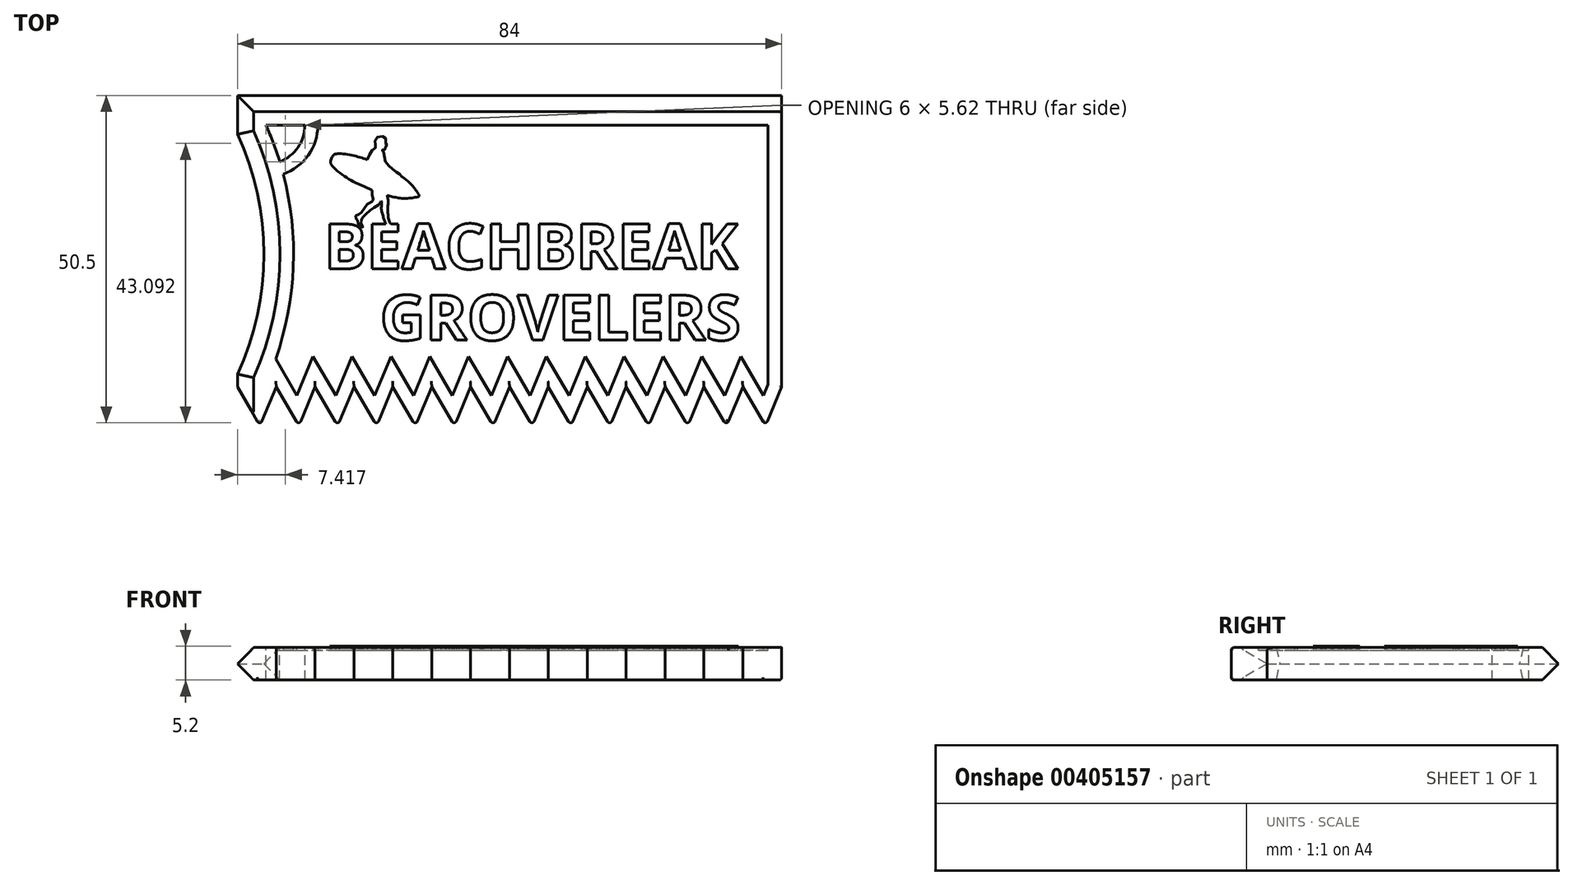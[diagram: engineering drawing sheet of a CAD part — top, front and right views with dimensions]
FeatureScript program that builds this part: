
annotation { "Feature Type Name" : "Feature", "Feature Type Description" : "" }
export const myFeature = defineFeature(function(context is Context, id is Id, definition is map)
    precondition{}
    {
        {
            assignVariable(context, id + "F0", {"name" : "t", "anyValue" : 2});
        }
        {
            var Q0;
            Q0=qCreatedBy(makeId("Top.planeOp"),FACE);
            var sketch = newSketch(context, id + "F1", { "sketchPlane" : qUnion([Q0])});
            skLineSegment(sketch, "E0.bottom", {"start": v(84, 51) * mm, "end": v(0, 51) * mm});
            skLineSegment(sketch, "E0.top", {"start": v(81.5, 0) * mm, "end": v(3.5, 0) * mm, "construction": true});
            skLineSegment(sketch, "E0.left", {"start": v(84, 51) * mm, "end": v(84, 6) * mm});
            skLineSegment(sketch, "E0.right", {"start": v(0, 51) * mm, "end": v(0, 6) * mm, "construction": true});
            skLineSegment(sketch, "E1", {"start": v(84, 6) * mm, "end": v(0, 6) * mm, "construction": true});
            skLineSegment(sketch, "E2", {"start": v(84, 6) * mm, "end": v(81.5, 0) * mm});
            skLineSegment(sketch, "E3", {"start": v(81.5, 0) * mm, "end": v(78, 6) * mm});
            skLineSegment(sketch, "E4.1.0.0", {"start": v(78, 6) * mm, "end": v(75.5, 0) * mm});
            skLineSegment(sketch, "E4.1.0.1", {"start": v(75.5, 0) * mm, "end": v(72, 6) * mm});
            skLineSegment(sketch, "E4.2.0.0", {"start": v(72, 6) * mm, "end": v(69.5, 0) * mm});
            skLineSegment(sketch, "E4.2.0.1", {"start": v(69.5, 0) * mm, "end": v(66, 6) * mm});
            skLineSegment(sketch, "E4.3.0.0", {"start": v(66, 6) * mm, "end": v(63.5, 0) * mm});
            skLineSegment(sketch, "E4.3.0.1", {"start": v(63.5, 0) * mm, "end": v(60, 6) * mm});
            skLineSegment(sketch, "E4.4.0.0", {"start": v(60, 6) * mm, "end": v(57.5, 0) * mm});
            skLineSegment(sketch, "E4.4.0.1", {"start": v(57.5, 0) * mm, "end": v(54, 6) * mm});
            skLineSegment(sketch, "E4.5.0.0", {"start": v(54, 6) * mm, "end": v(51.5, 0) * mm});
            skLineSegment(sketch, "E4.5.0.1", {"start": v(51.5, 0) * mm, "end": v(48, 6) * mm});
            skLineSegment(sketch, "E4.6.0.0", {"start": v(48, 6) * mm, "end": v(45.5, 0) * mm});
            skLineSegment(sketch, "E4.6.0.1", {"start": v(45.5, 0) * mm, "end": v(42, 6) * mm});
            skLineSegment(sketch, "E4.7.0.0", {"start": v(42, 6) * mm, "end": v(39.5, 0) * mm});
            skLineSegment(sketch, "E4.7.0.1", {"start": v(39.5, 0) * mm, "end": v(36, 6) * mm});
            skLineSegment(sketch, "E4.8.0.0", {"start": v(36, 6) * mm, "end": v(33.5, 0) * mm});
            skLineSegment(sketch, "E4.8.0.1", {"start": v(33.5, 0) * mm, "end": v(30, 6) * mm});
            skLineSegment(sketch, "E4.9.0.0", {"start": v(30, 6) * mm, "end": v(27.5, 0) * mm});
            skLineSegment(sketch, "E4.9.0.1", {"start": v(27.5, 0) * mm, "end": v(24, 6) * mm});
            skLineSegment(sketch, "E4.10.0.0", {"start": v(24, 6) * mm, "end": v(21.5, 0) * mm});
            skLineSegment(sketch, "E4.10.0.1", {"start": v(21.5, 0) * mm, "end": v(18, 6) * mm});
            skLineSegment(sketch, "E4.11.0.0", {"start": v(18, 6) * mm, "end": v(15.5, 0) * mm});
            skLineSegment(sketch, "E4.11.0.1", {"start": v(15.5, 0) * mm, "end": v(12, 6) * mm});
            skLineSegment(sketch, "E4.12.0.0", {"start": v(12, 6) * mm, "end": v(9.5, 0) * mm});
            skLineSegment(sketch, "E4.12.0.1", {"start": v(9.5, 0) * mm, "end": v(6, 6) * mm});
            skLineSegment(sketch, "E4.13.0.0", {"start": v(6, 6) * mm, "end": v(3.5, 0) * mm});
            skLineSegment(sketch, "E4.13.0.1", {"start": v(3.5, 0) * mm, "end": v(0, 6) * mm});
            skLineSegment(sketch, "E4.direction1", {"start": v(84, 6) * mm, "end": v(78, 6) * mm, "construction": true});
            skLineSegment(sketch, "E5", {"start": v(0, 6) * mm, "end": v(0, 8) * mm});
            skArc(sketch, "E6", {"start": v(0, 8) * mm, "mid": v(4.07, 26.5) * mm, "end": v(0, 45) * mm});
            skLineSegment(sketch, "E7", {"start": v(0, 45) * mm, "end": v(0, 51) * mm});
            skLineSegment(sketch, "E8", {"start": v(0, 6) * mm, "end": v(0, 0) * mm, "construction": true});
            skSolve(sketch);
        }
        {
            var Q0;
            Q0=qSketchRegion(id+"F1",true);
            extrude(context, id + "F2", {"entities" : qUnion([Q0]), "depth" : 5 * mm});
        }
        {
            var Q0;
            Q0=makeQuery(id+"F2.opExtrude","CAP_EDGE",EDGE,{"disambiguationData":[OSD([sQuery(id+"F1.wireOp",EDGE,"E5")])],"isStart":false});
            var Q1;
            Q1=makeQuery(id+"F2.opExtrude","CAP_EDGE",EDGE,{"disambiguationData":[OSD([sQuery(id+"F1.wireOp",EDGE,"E6")])],"isStart":false});
            var Q2;
            Q2=makeQuery(id+"F2.opExtrude","CAP_EDGE",EDGE,{"disambiguationData":[OSD([sQuery(id+"F1.wireOp",EDGE,"E0.bottom")])],"isStart":false});
            var Q3;
            Q3=makeQuery(id+"F2.opExtrude","CAP_EDGE",EDGE,{"disambiguationData":[OSD([sQuery(id+"F1.wireOp",EDGE,"E7")])],"isStart":false});
            var Q4;
            Q4=makeQuery(id+"F2.opExtrude","CAP_EDGE",EDGE,{"disambiguationData":[OSD([sQuery(id+"F1.wireOp",EDGE,"E0.bottom")])],"isStart":true});
            var Q5;
            Q5=makeQuery(id+"F2.opExtrude","CAP_EDGE",EDGE,{"disambiguationData":[OSD([sQuery(id+"F1.wireOp",EDGE,"E7")])],"isStart":true});
            var Q6;
            Q6=makeQuery(id+"F2.opExtrude","CAP_EDGE",EDGE,{"disambiguationData":[OSD([sQuery(id+"F1.wireOp",EDGE,"E6")])],"isStart":true});
            var Q7;
            Q7=makeQuery(id+"F2.opExtrude","CAP_EDGE",EDGE,{"disambiguationData":[OSD([sQuery(id+"F1.wireOp",EDGE,"E5")])],"isStart":true});
            chamfer(context, id + "F3", {"entities" : qUnion([Q0, Q1, Q2, Q3, Q4, Q5, Q6, Q7]), "chamferType" : ChamferType.TWO_OFFSETS, "width1" : 2.5 * mm, "oppositeDirection" : false, "width2" : 2.5 * mm, "tangentPropagation" : true});
        }
        {
            var Q0;
            Q0=makeQuery(id+"F2.opExtrude","CAP_FACE",FACE,{"disambiguationData":[OSD([sQuery(id+"F1.wireOp",EDGE,"E0.bottom"),sQuery(id+"F1.wireOp",EDGE,"E0.left"),sQuery(id+"F1.wireOp",EDGE,"E2"),sQuery(id+"F1.wireOp",EDGE,"E3"),sQuery(id+"F1.wireOp",EDGE,"E4.1.0.0"),sQuery(id+"F1.wireOp",EDGE,"E4.1.0.1"),sQuery(id+"F1.wireOp",EDGE,"E4.2.0.0"),sQuery(id+"F1.wireOp",EDGE,"E4.2.0.1"),sQuery(id+"F1.wireOp",EDGE,"E4.3.0.0"),sQuery(id+"F1.wireOp",EDGE,"E4.3.0.1"),sQuery(id+"F1.wireOp",EDGE,"E4.4.0.0"),sQuery(id+"F1.wireOp",EDGE,"E4.4.0.1"),sQuery(id+"F1.wireOp",EDGE,"E4.5.0.0"),sQuery(id+"F1.wireOp",EDGE,"E4.5.0.1"),sQuery(id+"F1.wireOp",EDGE,"E4.6.0.0"),sQuery(id+"F1.wireOp",EDGE,"E4.6.0.1"),sQuery(id+"F1.wireOp",EDGE,"E4.7.0.0"),sQuery(id+"F1.wireOp",EDGE,"E4.7.0.1"),sQuery(id+"F1.wireOp",EDGE,"E4.8.0.0"),sQuery(id+"F1.wireOp",EDGE,"E4.8.0.1"),sQuery(id+"F1.wireOp",EDGE,"E4.9.0.0"),sQuery(id+"F1.wireOp",EDGE,"E4.9.0.1"),sQuery(id+"F1.wireOp",EDGE,"E4.10.0.0"),sQuery(id+"F1.wireOp",EDGE,"E4.10.0.1"),sQuery(id+"F1.wireOp",EDGE,"E4.11.0.0"),sQuery(id+"F1.wireOp",EDGE,"E4.11.0.1"),sQuery(id+"F1.wireOp",EDGE,"E4.12.0.0"),sQuery(id+"F1.wireOp",EDGE,"E4.12.0.1"),sQuery(id+"F1.wireOp",EDGE,"E4.13.0.0"),sQuery(id+"F1.wireOp",EDGE,"E4.13.0.1"),sQuery(id+"F1.wireOp",EDGE,"E5"),sQuery(id+"F1.wireOp",EDGE,"E6"),sQuery(id+"F1.wireOp",EDGE,"E7")])],"isStart":false});
            var sketch = newSketch(context, id + "F4", { "sketchPlane" : qUnion([Q0])});
            skLineSegment(sketch, "E9.0", {"start": v(81.9, 6.42) * mm, "end": v(81.9, 46.4) * mm});
            skLineSegment(sketch, "E9.1", {"start": v(81.19, 4.7) * mm, "end": v(81.9, 6.42) * mm});
            skLineSegment(sketch, "E9.2", {"start": v(77.69, 10.7) * mm, "end": v(81.19, 4.7) * mm});
            skLineSegment(sketch, "E9.3", {"start": v(75.19, 4.7) * mm, "end": v(77.69, 10.7) * mm});
            skLineSegment(sketch, "E9.4", {"start": v(71.69, 10.7) * mm, "end": v(75.19, 4.7) * mm});
            skLineSegment(sketch, "E9.5", {"start": v(69.19, 4.7) * mm, "end": v(71.69, 10.7) * mm});
            skLineSegment(sketch, "E9.6", {"start": v(65.69, 10.7) * mm, "end": v(69.19, 4.7) * mm});
            skLineSegment(sketch, "E9.7", {"start": v(81.9, 46.4) * mm, "end": v(4.42, 46.4) * mm});
            skArc(sketch, "E9.8", {"start": v(4.42, 46.4) * mm, "mid": v(8.63, 28.5) * mm, "end": v(5.9, 10.33) * mm});
            skLineSegment(sketch, "E9.9", {"start": v(5.9, 10.33) * mm, "end": v(9.19, 4.7) * mm});
            skLineSegment(sketch, "E9.10", {"start": v(9.19, 4.7) * mm, "end": v(11.69, 10.7) * mm});
            skLineSegment(sketch, "E9.11", {"start": v(11.69, 10.7) * mm, "end": v(15.19, 4.7) * mm});
            skLineSegment(sketch, "E9.12", {"start": v(15.19, 4.7) * mm, "end": v(17.69, 10.7) * mm});
            skLineSegment(sketch, "E9.13", {"start": v(17.69, 10.7) * mm, "end": v(21.19, 4.7) * mm});
            skLineSegment(sketch, "E9.14", {"start": v(21.19, 4.7) * mm, "end": v(23.69, 10.7) * mm});
            skLineSegment(sketch, "E9.15", {"start": v(23.69, 10.7) * mm, "end": v(27.19, 4.7) * mm});
            skLineSegment(sketch, "E9.16", {"start": v(27.19, 4.7) * mm, "end": v(29.69, 10.7) * mm});
            skLineSegment(sketch, "E9.17", {"start": v(29.69, 10.7) * mm, "end": v(33.19, 4.7) * mm});
            skLineSegment(sketch, "E9.18", {"start": v(33.19, 4.7) * mm, "end": v(35.69, 10.7) * mm});
            skLineSegment(sketch, "E9.19", {"start": v(35.69, 10.7) * mm, "end": v(39.19, 4.7) * mm});
            skLineSegment(sketch, "E9.20", {"start": v(39.19, 4.7) * mm, "end": v(41.69, 10.7) * mm});
            skLineSegment(sketch, "E9.21", {"start": v(41.69, 10.7) * mm, "end": v(45.19, 4.7) * mm});
            skLineSegment(sketch, "E9.22", {"start": v(45.19, 4.7) * mm, "end": v(47.69, 10.7) * mm});
            skLineSegment(sketch, "E9.23", {"start": v(47.69, 10.7) * mm, "end": v(51.19, 4.7) * mm});
            skLineSegment(sketch, "E9.24", {"start": v(51.19, 4.7) * mm, "end": v(53.69, 10.7) * mm});
            skLineSegment(sketch, "E9.25", {"start": v(53.69, 10.7) * mm, "end": v(57.19, 4.7) * mm});
            skLineSegment(sketch, "E9.26", {"start": v(57.19, 4.7) * mm, "end": v(59.69, 10.7) * mm});
            skLineSegment(sketch, "E9.27", {"start": v(59.69, 10.7) * mm, "end": v(63.19, 4.7) * mm});
            skLineSegment(sketch, "E9.28", {"start": v(63.19, 4.7) * mm, "end": v(65.69, 10.7) * mm});
            skSolve(sketch);
        }
        {
            var Q0;
            Q0=makeQuery(id+"F4.imprint","IMPRINT",FACE,{"disambiguationData":[TD([[makeQuery(id+"F4.imprint","IMPRINT",EDGE,{"derivedFrom":sQuery(id+"F4.wireOp",EDGE,"E9.0")}),1.0]])]});
            extrude(context, id + "F5", {"entities" : qUnion([Q0]), "operationType" : NewBodyOperationType.REMOVE, "oppositeDirection" : true, "depth" : (getVariable(context, 't') / 5) * mm});
        }
        {
            var Q0;
            Q0=makeQuery(id+"F2.opExtrude","CAP_EDGE",EDGE,{"disambiguationData":[OSD([sQuery(id+"F1.wireOp",EDGE,"E4.13.0.1")])],"isStart":false});
            var Q1;
            Q1=makeQuery(id+"F2.opExtrude","CAP_EDGE",EDGE,{"disambiguationData":[OSD([sQuery(id+"F1.wireOp",EDGE,"E4.13.0.0")])],"isStart":false});
            var Q2;
            Q2=makeQuery(id+"F2.opExtrude","SWEPT_EDGE",EDGE,{"disambiguationData":[OSD([sQuery(id+"F1.wireOp",EDGE,"E4.13.0.0"),sQuery(id+"F1.wireOp",EDGE,"E4.13.0.1")])]});
            var Q3;
            Q3=makeQuery(id+"F2.opExtrude","CAP_EDGE",EDGE,{"disambiguationData":[OSD([sQuery(id+"F1.wireOp",EDGE,"E4.12.0.1")])],"isStart":false});
            var Q4;
            Q4=makeQuery(id+"F2.opExtrude","SWEPT_EDGE",EDGE,{"disambiguationData":[OSD([sQuery(id+"F1.wireOp",EDGE,"E4.12.0.0"),sQuery(id+"F1.wireOp",EDGE,"E4.12.0.1")])]});
            var Q5;
            Q5=makeQuery(id+"F2.opExtrude","CAP_EDGE",EDGE,{"disambiguationData":[OSD([sQuery(id+"F1.wireOp",EDGE,"E4.12.0.0")])],"isStart":false});
            var Q6;
            Q6=makeQuery(id+"F2.opExtrude","CAP_EDGE",EDGE,{"disambiguationData":[OSD([sQuery(id+"F1.wireOp",EDGE,"E4.11.0.1")])],"isStart":false});
            var Q7;
            Q7=makeQuery(id+"F2.opExtrude","SWEPT_EDGE",EDGE,{"disambiguationData":[OSD([sQuery(id+"F1.wireOp",EDGE,"E4.11.0.0"),sQuery(id+"F1.wireOp",EDGE,"E4.11.0.1")])]});
            var Q8;
            Q8=makeQuery(id+"F2.opExtrude","CAP_EDGE",EDGE,{"disambiguationData":[OSD([sQuery(id+"F1.wireOp",EDGE,"E4.11.0.0")])],"isStart":false});
            var Q9;
            Q9=makeQuery(id+"F2.opExtrude","CAP_EDGE",EDGE,{"disambiguationData":[OSD([sQuery(id+"F1.wireOp",EDGE,"E4.10.0.1")])],"isStart":false});
            var Q10;
            Q10=makeQuery(id+"F2.opExtrude","CAP_EDGE",EDGE,{"disambiguationData":[OSD([sQuery(id+"F1.wireOp",EDGE,"E4.10.0.0")])],"isStart":false});
            var Q11;
            Q11=makeQuery(id+"F2.opExtrude","CAP_EDGE",EDGE,{"disambiguationData":[OSD([sQuery(id+"F1.wireOp",EDGE,"E4.9.0.1")])],"isStart":false});
            var Q12;
            Q12=makeQuery(id+"F2.opExtrude","CAP_EDGE",EDGE,{"disambiguationData":[OSD([sQuery(id+"F1.wireOp",EDGE,"E4.9.0.0")])],"isStart":false});
            var Q13;
            Q13=makeQuery(id+"F2.opExtrude","CAP_EDGE",EDGE,{"disambiguationData":[OSD([sQuery(id+"F1.wireOp",EDGE,"E4.8.0.1")])],"isStart":false});
            var Q14;
            Q14=makeQuery(id+"F2.opExtrude","CAP_EDGE",EDGE,{"disambiguationData":[OSD([sQuery(id+"F1.wireOp",EDGE,"E4.8.0.0")])],"isStart":false});
            var Q15;
            Q15=makeQuery(id+"F2.opExtrude","CAP_EDGE",EDGE,{"disambiguationData":[OSD([sQuery(id+"F1.wireOp",EDGE,"E4.7.0.1")])],"isStart":false});
            var Q16;
            Q16=makeQuery(id+"F2.opExtrude","CAP_EDGE",EDGE,{"disambiguationData":[OSD([sQuery(id+"F1.wireOp",EDGE,"E4.7.0.0")])],"isStart":false});
            var Q17;
            Q17=makeQuery(id+"F2.opExtrude","CAP_EDGE",EDGE,{"disambiguationData":[OSD([sQuery(id+"F1.wireOp",EDGE,"E4.6.0.1")])],"isStart":false});
            var Q18;
            Q18=makeQuery(id+"F2.opExtrude","CAP_EDGE",EDGE,{"disambiguationData":[OSD([sQuery(id+"F1.wireOp",EDGE,"E4.6.0.0")])],"isStart":false});
            var Q19;
            Q19=makeQuery(id+"F2.opExtrude","CAP_EDGE",EDGE,{"disambiguationData":[OSD([sQuery(id+"F1.wireOp",EDGE,"E4.5.0.1")])],"isStart":false});
            var Q20;
            Q20=makeQuery(id+"F2.opExtrude","CAP_EDGE",EDGE,{"disambiguationData":[OSD([sQuery(id+"F1.wireOp",EDGE,"E4.5.0.0")])],"isStart":false});
            var Q21;
            Q21=makeQuery(id+"F2.opExtrude","CAP_EDGE",EDGE,{"disambiguationData":[OSD([sQuery(id+"F1.wireOp",EDGE,"E4.4.0.1")])],"isStart":false});
            var Q22;
            Q22=makeQuery(id+"F2.opExtrude","CAP_EDGE",EDGE,{"disambiguationData":[OSD([sQuery(id+"F1.wireOp",EDGE,"E4.4.0.0")])],"isStart":false});
            var Q23;
            Q23=makeQuery(id+"F2.opExtrude","CAP_EDGE",EDGE,{"disambiguationData":[OSD([sQuery(id+"F1.wireOp",EDGE,"E4.3.0.1")])],"isStart":false});
            var Q24;
            Q24=makeQuery(id+"F2.opExtrude","CAP_EDGE",EDGE,{"disambiguationData":[OSD([sQuery(id+"F1.wireOp",EDGE,"E4.3.0.0")])],"isStart":false});
            var Q25;
            Q25=makeQuery(id+"F2.opExtrude","CAP_EDGE",EDGE,{"disambiguationData":[OSD([sQuery(id+"F1.wireOp",EDGE,"E4.2.0.1")])],"isStart":false});
            var Q26;
            Q26=makeQuery(id+"F2.opExtrude","CAP_EDGE",EDGE,{"disambiguationData":[OSD([sQuery(id+"F1.wireOp",EDGE,"E4.2.0.0")])],"isStart":false});
            var Q27;
            Q27=makeQuery(id+"F2.opExtrude","CAP_EDGE",EDGE,{"disambiguationData":[OSD([sQuery(id+"F1.wireOp",EDGE,"E4.1.0.1")])],"isStart":false});
            var Q28;
            Q28=makeQuery(id+"F2.opExtrude","CAP_EDGE",EDGE,{"disambiguationData":[OSD([sQuery(id+"F1.wireOp",EDGE,"E4.1.0.0")])],"isStart":false});
            var Q29;
            Q29=makeQuery(id+"F2.opExtrude","CAP_EDGE",EDGE,{"disambiguationData":[OSD([sQuery(id+"F1.wireOp",EDGE,"E3")])],"isStart":false});
            var Q30;
            Q30=makeQuery(id+"F2.opExtrude","SWEPT_EDGE",EDGE,{"disambiguationData":[OSD([sQuery(id+"F1.wireOp",EDGE,"E2"),sQuery(id+"F1.wireOp",EDGE,"E3")])]});
            var Q31;
            Q31=makeQuery(id+"F2.opExtrude","CAP_EDGE",EDGE,{"disambiguationData":[OSD([sQuery(id+"F1.wireOp",EDGE,"E2")])],"isStart":false});
            var Q32;
            Q32=makeQuery(id+"F2.opExtrude","SWEPT_EDGE",EDGE,{"disambiguationData":[OSD([sQuery(id+"F1.wireOp",EDGE,"E4.1.0.0"),sQuery(id+"F1.wireOp",EDGE,"E4.1.0.1")])]});
            var Q33;
            Q33=makeQuery(id+"F2.opExtrude","SWEPT_EDGE",EDGE,{"disambiguationData":[OSD([sQuery(id+"F1.wireOp",EDGE,"E4.2.0.0"),sQuery(id+"F1.wireOp",EDGE,"E4.2.0.1")])]});
            var Q34;
            Q34=makeQuery(id+"F2.opExtrude","SWEPT_EDGE",EDGE,{"disambiguationData":[OSD([sQuery(id+"F1.wireOp",EDGE,"E4.3.0.0"),sQuery(id+"F1.wireOp",EDGE,"E4.3.0.1")])]});
            var Q35;
            Q35=makeQuery(id+"F2.opExtrude","SWEPT_EDGE",EDGE,{"disambiguationData":[OSD([sQuery(id+"F1.wireOp",EDGE,"E4.4.0.0"),sQuery(id+"F1.wireOp",EDGE,"E4.4.0.1")])]});
            var Q36;
            Q36=makeQuery(id+"F2.opExtrude","SWEPT_EDGE",EDGE,{"disambiguationData":[OSD([sQuery(id+"F1.wireOp",EDGE,"E4.5.0.0"),sQuery(id+"F1.wireOp",EDGE,"E4.5.0.1")])]});
            var Q37;
            Q37=makeQuery(id+"F2.opExtrude","SWEPT_EDGE",EDGE,{"disambiguationData":[OSD([sQuery(id+"F1.wireOp",EDGE,"E4.6.0.0"),sQuery(id+"F1.wireOp",EDGE,"E4.6.0.1")])]});
            var Q38;
            Q38=makeQuery(id+"F2.opExtrude","SWEPT_EDGE",EDGE,{"disambiguationData":[OSD([sQuery(id+"F1.wireOp",EDGE,"E4.7.0.0"),sQuery(id+"F1.wireOp",EDGE,"E4.7.0.1")])]});
            var Q39;
            Q39=makeQuery(id+"F2.opExtrude","SWEPT_EDGE",EDGE,{"disambiguationData":[OSD([sQuery(id+"F1.wireOp",EDGE,"E4.8.0.0"),sQuery(id+"F1.wireOp",EDGE,"E4.8.0.1")])]});
            var Q40;
            Q40=makeQuery(id+"F2.opExtrude","SWEPT_EDGE",EDGE,{"disambiguationData":[OSD([sQuery(id+"F1.wireOp",EDGE,"E4.9.0.0"),sQuery(id+"F1.wireOp",EDGE,"E4.9.0.1")])]});
            var Q41;
            Q41=makeQuery(id+"F2.opExtrude","SWEPT_EDGE",EDGE,{"disambiguationData":[OSD([sQuery(id+"F1.wireOp",EDGE,"E4.10.0.0"),sQuery(id+"F1.wireOp",EDGE,"E4.10.0.1")])]});
            var Q42;
            Q42=makeQuery(id+"F2.opExtrude","CAP_FACE",FACE,{"disambiguationData":[OSD([sQuery(id+"F1.wireOp",EDGE,"E0.bottom"),sQuery(id+"F1.wireOp",EDGE,"E0.left"),sQuery(id+"F1.wireOp",EDGE,"E2"),sQuery(id+"F1.wireOp",EDGE,"E3"),sQuery(id+"F1.wireOp",EDGE,"E4.1.0.0"),sQuery(id+"F1.wireOp",EDGE,"E4.1.0.1"),sQuery(id+"F1.wireOp",EDGE,"E4.2.0.0"),sQuery(id+"F1.wireOp",EDGE,"E4.2.0.1"),sQuery(id+"F1.wireOp",EDGE,"E4.3.0.0"),sQuery(id+"F1.wireOp",EDGE,"E4.3.0.1"),sQuery(id+"F1.wireOp",EDGE,"E4.4.0.0"),sQuery(id+"F1.wireOp",EDGE,"E4.4.0.1"),sQuery(id+"F1.wireOp",EDGE,"E4.5.0.0"),sQuery(id+"F1.wireOp",EDGE,"E4.5.0.1"),sQuery(id+"F1.wireOp",EDGE,"E4.6.0.0"),sQuery(id+"F1.wireOp",EDGE,"E4.6.0.1"),sQuery(id+"F1.wireOp",EDGE,"E4.7.0.0"),sQuery(id+"F1.wireOp",EDGE,"E4.7.0.1"),sQuery(id+"F1.wireOp",EDGE,"E4.8.0.0"),sQuery(id+"F1.wireOp",EDGE,"E4.8.0.1"),sQuery(id+"F1.wireOp",EDGE,"E4.9.0.0"),sQuery(id+"F1.wireOp",EDGE,"E4.9.0.1"),sQuery(id+"F1.wireOp",EDGE,"E4.10.0.0"),sQuery(id+"F1.wireOp",EDGE,"E4.10.0.1"),sQuery(id+"F1.wireOp",EDGE,"E4.11.0.0"),sQuery(id+"F1.wireOp",EDGE,"E4.11.0.1"),sQuery(id+"F1.wireOp",EDGE,"E4.12.0.0"),sQuery(id+"F1.wireOp",EDGE,"E4.12.0.1"),sQuery(id+"F1.wireOp",EDGE,"E4.13.0.0"),sQuery(id+"F1.wireOp",EDGE,"E4.13.0.1"),sQuery(id+"F1.wireOp",EDGE,"E5"),sQuery(id+"F1.wireOp",EDGE,"E6"),sQuery(id+"F1.wireOp",EDGE,"E7")])],"isStart":true});
            fillet(context, id + "F6", {"entities" : qUnion([Q0, Q1, Q2, Q3, Q4, Q5, Q6, Q7, Q8, Q9, Q10, Q11, Q12, Q13, Q14, Q15, Q16, Q17, Q18, Q19, Q20, Q21, Q22, Q23, Q24, Q25, Q26, Q27, Q28, Q29, Q30, Q31, Q32, Q33, Q34, Q35, Q36, Q37, Q38, Q39, Q40, Q41, Q42]), "radius" : .4 * mm, "tangentPropagation" : true, "allowEdgeOverflow" : false});
        }
        {
            var Q0;
            Q0=makeQuery(id+"F5.boolean.opBoolean","COPY",FACE,{"derivedFrom":makeQuery(id+"F5.opExtrude","CAP_FACE",FACE,{"disambiguationData":[OSD([sQuery(id+"F4.wireOp",EDGE,"E9.0"),sQuery(id+"F4.wireOp",EDGE,"E9.1"),sQuery(id+"F4.wireOp",EDGE,"E9.2"),sQuery(id+"F4.wireOp",EDGE,"E9.3"),sQuery(id+"F4.wireOp",EDGE,"E9.4"),sQuery(id+"F4.wireOp",EDGE,"E9.5"),sQuery(id+"F4.wireOp",EDGE,"E9.6"),sQuery(id+"F4.wireOp",EDGE,"E9.7"),sQuery(id+"F4.wireOp",EDGE,"E9.8"),sQuery(id+"F4.wireOp",EDGE,"E9.9"),sQuery(id+"F4.wireOp",EDGE,"E9.10"),sQuery(id+"F4.wireOp",EDGE,"E9.11"),sQuery(id+"F4.wireOp",EDGE,"E9.12"),sQuery(id+"F4.wireOp",EDGE,"E9.13"),sQuery(id+"F4.wireOp",EDGE,"E9.14"),sQuery(id+"F4.wireOp",EDGE,"E9.15"),sQuery(id+"F4.wireOp",EDGE,"E9.16"),sQuery(id+"F4.wireOp",EDGE,"E9.17"),sQuery(id+"F4.wireOp",EDGE,"E9.18"),sQuery(id+"F4.wireOp",EDGE,"E9.19"),sQuery(id+"F4.wireOp",EDGE,"E9.20"),sQuery(id+"F4.wireOp",EDGE,"E9.21"),sQuery(id+"F4.wireOp",EDGE,"E9.22"),sQuery(id+"F4.wireOp",EDGE,"E9.23"),sQuery(id+"F4.wireOp",EDGE,"E9.24"),sQuery(id+"F4.wireOp",EDGE,"E9.25"),sQuery(id+"F4.wireOp",EDGE,"E9.26"),sQuery(id+"F4.wireOp",EDGE,"E9.27"),sQuery(id+"F4.wireOp",EDGE,"E9.28")])],"isStart":false})});
            var sketch = newSketch(context, id + "F7", { "sketchPlane" : qUnion([Q0])});
            skText(sketch, "E10", { "text": "GROVELERS", "fontName": "OpenSans-Bold.ttf"});
            skText(sketch, "E11", { "text": "BEACHBREAK", "fontName": "OpenSans-Bold.ttf"});
            const initialGuessF7  = {"E10": [0.02199, 0.01323, 1, 0, 0.007], "E11": [0.0134, 0.02423, 1, 0, 0.007]};
            skSetInitialGuess(sketch, initialGuessF7);
            skSolve(sketch);
        }
        {
            var Q0;
            Q0=makeQuery(id+"F7.imprint","IMPRINT",FACE,{"disambiguationData":[TD([[makeQuery(id+"F7.imprint","IMPRINT",EDGE,{"derivedFrom":sQuery(id+"F7.wireOp",EDGE,"E10.sketch_text.stroke-0")}),1.0]])]});
            var sketch = newSketch(context, id + "F8", { "sketchPlane" : qUnion([Q0])});
            skLineSegment(sketch, "E12.0", {"start": v(81.9, 46.4) * mm, "end": v(4.42, 46.4) * mm});
            skArc(sketch, "E12.1", {"start": v(4.42, 46.4) * mm, "mid": v(8.63, 28.5) * mm, "end": v(5.9, 10.33) * mm});
            skPoint(sketch, "E12.2", {"position": v(4.42, 46.4) * mm});
            skArc(sketch, "E13", {"start": v(6.53, 40.78) * mm, "mid": v(9.35, 42.98) * mm, "end": v(10.42, 46.4) * mm});
            skArc(sketch, "E14", {"start": v(7.08, 38.86) * mm, "mid": v(10.95, 41.78) * mm, "end": v(12.42, 46.4) * mm});
            skLineSegment(sketch, "E15", {"start": v(14.33, 41.37) * mm, "end": v(28.35, 35.34) * mm, "construction": true});
            skFitSpline(sketch, "E16", {"points": [v(20.78, 36.4) * mm, v(18.17, 37.57) * mm, v(16.2, 38.77) * mm, v(14.57, 40.2) * mm, v(14.39, 40.75) * mm, v(14.51, 41.3) * mm], "startDerivative": vector(-8.18, 3.62) * mm, "endDerivative": vector(1.44, 4.42) * mm});
            skFitSpline(sketch, "E17", {"points": [v(21.8, 40.38) * mm, v(19.73, 41.2) * mm, v(17.5, 41.8) * mm, v(15.34, 42) * mm, v(14.82, 41.76) * mm, v(14.51, 41.3) * mm], "startDerivative": vector(-8.26, 3.44) * mm, "endDerivative": vector(-2.21, -4.08) * mm});
            skFitSpline(sketch, "E18", {"points": [v(20.78, 36.4) * mm, v(20.78, 35.64) * mm, v(20.95, 35.07) * mm, v(20.96, 34.8) * mm, v(20.8, 34.66) * mm, v(20.25, 34.4) * mm, v(19.79, 33.88) * mm, v(19.35, 33.26) * mm, v(19, 32.82) * mm, v(18.79, 32.65) * mm, v(18.48, 32.52) * mm, v(18.27, 32.44) * mm, v(18.2, 32.27) * mm, v(18.32, 31.93) * mm, v(18.48, 31.77) * mm, v(18.61, 31.65) * mm, v(18.65, 31.45) * mm, v(18.68, 31.05) * mm, v(18.84, 30.85) * mm, v(19.05, 30.74) * mm, v(19.33, 30.68) * mm, v(19.38, 30.7) * mm, v(19.39, 30.75) * mm, v(19.36, 30.83) * mm, v(19.24, 30.92) * mm, v(19.13, 31.03) * mm, v(19.11, 31.31) * mm, v(19.14, 31.62) * mm, v(19.17, 31.85) * mm, v(19.25, 32.01) * mm, v(19.45, 32.31) * mm, v(19.98, 32.83) * mm, v(20.57, 33.32) * mm, v(21.18, 33.76) * mm, v(21.73, 34.08) * mm, v(21.96, 34.28) * mm, v(22.05, 34.5) * mm, v(22.1, 34.7) * mm, v(22.15, 34.73) * mm, v(22.18, 34.73) * mm], "startDerivative": vector(-1.7, -19.21) * mm, "endDerivative": vector(3.01, -1.59) * mm});
            skFitSpline(sketch, "E19", {"points": [v(20.05, 41.08) * mm, v(20.31, 41.73) * mm, v(20.57, 42.25) * mm, v(20.85, 42.54) * mm, v(21.15, 42.79) * mm, v(21.36, 42.97) * mm, v(21.42, 43.1) * mm, v(21.3, 43.35) * mm, v(21.2, 43.69) * mm, v(21.26, 44.09) * mm, v(21.42, 44.41) * mm, v(21.96, 44.72) * mm, v(22.41, 44.65) * mm, v(22.73, 44.52) * mm, v(22.95, 44.3) * mm, v(22.93, 44.07) * mm, v(22.87, 43.95) * mm, v(22.93, 43.83) * mm, v(22.96, 43.68) * mm, v(22.91, 43.6) * mm, v(22.9, 43.54) * mm, v(22.98, 43.43) * mm, v(23.06, 43.31) * mm, v(23.06, 43.23) * mm, v(23.02, 43.17) * mm, v(22.9, 43.2) * mm, v(22.89, 43.13) * mm, v(22.89, 43.03) * mm, v(22.86, 42.96) * mm, v(22.81, 42.9) * mm, v(22.82, 42.8) * mm, v(22.85, 42.72) * mm, v(22.83, 42.65) * mm, v(22.74, 42.62) * mm, v(22.65, 42.58) * mm, v(22.47, 42.6) * mm, v(22.37, 42.6) * mm, v(22.3, 42.56) * mm, v(22.37, 42.46) * mm, v(22.53, 42.3) * mm, v(22.67, 41.97) * mm, v(22.68, 41.44) * mm, v(22.8, 40.96) * mm, v(23.02, 40.5) * mm, v(23.5, 40.04) * mm, v(23.89, 39.68) * mm, v(24.31, 39.38) * mm, v(24.62, 39.05) * mm, v(24.88, 38.93) * mm, v(25.2, 38.8) * mm, v(25.31, 38.6) * mm, v(25.34, 38.5) * mm], "startDerivative": vector(7.84, 19.36) * mm, "endDerivative": vector(2.4, -8.81) * mm});
            skFitSpline(sketch, "E20", {"points": [v(23.11, 35.6) * mm, v(23.77, 35.42) * mm, v(24.73, 35.21) * mm, v(25.68, 35.1) * mm, v(26.5, 35.15) * mm, v(27.4, 35.27) * mm, v(28.03, 35.44) * mm, v(28.05, 35.47) * mm], "startDerivative": vector(4.26, -1.27) * mm, "endDerivative": vector(0.24, 0.98) * mm});
            skFitSpline(sketch, "E21.MirrorCS", {"points": [v(24.56, 38.97) * mm, v(25.15, 38.62) * mm, v(25.96, 38.06) * mm, v(26.68, 37.45) * mm, v(27.23, 36.82) * mm, v(27.75, 36.09) * mm, v(28.06, 35.52) * mm, v(28.05, 35.47) * mm], "startDerivative": vector(3.85, -2.22) * mm, "endDerivative": vector(-0.55, -0.85) * mm});
            skFitSpline(sketch, "E22", {"points": [v(23.11, 35.6) * mm, v(23.22, 35.14) * mm, v(23.28, 34.82) * mm, v(23.26, 34.39) * mm, v(23.22, 33.76) * mm, v(23.23, 33.07) * mm, v(23.28, 32.27) * mm, v(23.41, 31.6) * mm, v(23.57, 31.3) * mm, v(23.85, 31.1) * mm, v(24.16, 31.01) * mm, v(24.42, 30.98) * mm, v(24.63, 30.93) * mm, v(24.73, 30.83) * mm, v(24.73, 30.75) * mm, v(24.68, 30.67) * mm, v(24.57, 30.62) * mm, v(24.4, 30.58) * mm, v(24.1, 30.57) * mm, v(23.65, 30.57) * mm, v(23.34, 30.59) * mm, v(23.1, 30.58) * mm, v(22.93, 30.59) * mm, v(22.84, 30.63) * mm, v(22.8, 30.76) * mm, v(22.8, 30.93) * mm, v(22.87, 31.1) * mm, v(22.87, 31.29) * mm, v(22.75, 31.62) * mm, v(22.54, 32.2) * mm, v(22.35, 32.86) * mm, v(22.2, 33.51) * mm, v(22.26, 34.1) * mm, v(22.28, 34.5) * mm, v(22.26, 34.67) * mm, v(22.18, 34.73) * mm], "startDerivative": vector(2.94, -13.83) * mm, "endDerivative": vector(-5.6, 2.93) * mm});
            skSolve(sketch);
        }
        {
            var Q0;
            Q0=qSketchRegion(id+"F7",true);
            var Q1;
            Q1=makeQuery(id+"F2.opExtrude","CAP_FACE",FACE,{"disambiguationData":[OSD([sQuery(id+"F1.wireOp",EDGE,"E0.bottom"),sQuery(id+"F1.wireOp",EDGE,"E0.left"),sQuery(id+"F1.wireOp",EDGE,"E2"),sQuery(id+"F1.wireOp",EDGE,"E3"),sQuery(id+"F1.wireOp",EDGE,"E4.1.0.0"),sQuery(id+"F1.wireOp",EDGE,"E4.1.0.1"),sQuery(id+"F1.wireOp",EDGE,"E4.2.0.0"),sQuery(id+"F1.wireOp",EDGE,"E4.2.0.1"),sQuery(id+"F1.wireOp",EDGE,"E4.3.0.0"),sQuery(id+"F1.wireOp",EDGE,"E4.3.0.1"),sQuery(id+"F1.wireOp",EDGE,"E4.4.0.0"),sQuery(id+"F1.wireOp",EDGE,"E4.4.0.1"),sQuery(id+"F1.wireOp",EDGE,"E4.5.0.0"),sQuery(id+"F1.wireOp",EDGE,"E4.5.0.1"),sQuery(id+"F1.wireOp",EDGE,"E4.6.0.0"),sQuery(id+"F1.wireOp",EDGE,"E4.6.0.1"),sQuery(id+"F1.wireOp",EDGE,"E4.7.0.0"),sQuery(id+"F1.wireOp",EDGE,"E4.7.0.1"),sQuery(id+"F1.wireOp",EDGE,"E4.8.0.0"),sQuery(id+"F1.wireOp",EDGE,"E4.8.0.1"),sQuery(id+"F1.wireOp",EDGE,"E4.9.0.0"),sQuery(id+"F1.wireOp",EDGE,"E4.9.0.1"),sQuery(id+"F1.wireOp",EDGE,"E4.10.0.0"),sQuery(id+"F1.wireOp",EDGE,"E4.10.0.1"),sQuery(id+"F1.wireOp",EDGE,"E4.11.0.0"),sQuery(id+"F1.wireOp",EDGE,"E4.11.0.1"),sQuery(id+"F1.wireOp",EDGE,"E4.12.0.0"),sQuery(id+"F1.wireOp",EDGE,"E4.12.0.1"),sQuery(id+"F1.wireOp",EDGE,"E4.13.0.0"),sQuery(id+"F1.wireOp",EDGE,"E4.13.0.1"),sQuery(id+"F1.wireOp",EDGE,"E5"),sQuery(id+"F1.wireOp",EDGE,"E6"),sQuery(id+"F1.wireOp",EDGE,"E7")])],"isStart":false});
            extrude(context, id + "F9", {"entities" : qUnion([Q0]), "operationType" : NewBodyOperationType.ADD, "endBoundEntityFace" : qUnion([Q1]), "depth" : .6 * mm});
        }
        {
            var Q0;
            {var subQ3=sQuery(id+"F8.wireOp",EDGE,"E13");Q0=makeQuery(id+"F8.imprint","IMPRINT",FACE,{"disambiguationData":[TD([[makeQuery(id+"F8.imprint","IMPRINT",EDGE,{"derivedFrom":subQ3}),1.0]])]});}
            extrude(context, id + "F10", {"entities" : qUnion([Q0]), "operationType" : NewBodyOperationType.REMOVE, "oppositeDirection" : true, "depth" : 25 * mm});
        }
        {
            var Q0;
            {var subQ0=sQuery(id+"F8.wireOp",EDGE,"E13");Q0=makeQuery(id+"F8.imprint","IMPRINT",FACE,{"disambiguationData":[TD([[makeQuery(id+"F8.imprint","IMPRINT",EDGE,{"derivedFrom":subQ0}),-1.0]])]});}
            var Q1;
            Q1=makeQuery(id+"F2.opExtrude","CAP_FACE",FACE,{"disambiguationData":[OSD([sQuery(id+"F1.wireOp",EDGE,"E0.bottom"),sQuery(id+"F1.wireOp",EDGE,"E0.left"),sQuery(id+"F1.wireOp",EDGE,"E2"),sQuery(id+"F1.wireOp",EDGE,"E3"),sQuery(id+"F1.wireOp",EDGE,"E4.1.0.0"),sQuery(id+"F1.wireOp",EDGE,"E4.1.0.1"),sQuery(id+"F1.wireOp",EDGE,"E4.2.0.0"),sQuery(id+"F1.wireOp",EDGE,"E4.2.0.1"),sQuery(id+"F1.wireOp",EDGE,"E4.3.0.0"),sQuery(id+"F1.wireOp",EDGE,"E4.3.0.1"),sQuery(id+"F1.wireOp",EDGE,"E4.4.0.0"),sQuery(id+"F1.wireOp",EDGE,"E4.4.0.1"),sQuery(id+"F1.wireOp",EDGE,"E4.5.0.0"),sQuery(id+"F1.wireOp",EDGE,"E4.5.0.1"),sQuery(id+"F1.wireOp",EDGE,"E4.6.0.0"),sQuery(id+"F1.wireOp",EDGE,"E4.6.0.1"),sQuery(id+"F1.wireOp",EDGE,"E4.7.0.0"),sQuery(id+"F1.wireOp",EDGE,"E4.7.0.1"),sQuery(id+"F1.wireOp",EDGE,"E4.8.0.0"),sQuery(id+"F1.wireOp",EDGE,"E4.8.0.1"),sQuery(id+"F1.wireOp",EDGE,"E4.9.0.0"),sQuery(id+"F1.wireOp",EDGE,"E4.9.0.1"),sQuery(id+"F1.wireOp",EDGE,"E4.10.0.0"),sQuery(id+"F1.wireOp",EDGE,"E4.10.0.1"),sQuery(id+"F1.wireOp",EDGE,"E4.11.0.0"),sQuery(id+"F1.wireOp",EDGE,"E4.11.0.1"),sQuery(id+"F1.wireOp",EDGE,"E4.12.0.0"),sQuery(id+"F1.wireOp",EDGE,"E4.12.0.1"),sQuery(id+"F1.wireOp",EDGE,"E4.13.0.0"),sQuery(id+"F1.wireOp",EDGE,"E4.13.0.1"),sQuery(id+"F1.wireOp",EDGE,"E5"),sQuery(id+"F1.wireOp",EDGE,"E6"),sQuery(id+"F1.wireOp",EDGE,"E7")])],"isStart":false});
            extrude(context, id + "F11", {"entities" : qUnion([Q0]), "operationType" : NewBodyOperationType.ADD, "endBound" : BoundingType.UP_TO_SURFACE, "endBoundEntityFace" : qUnion([Q1]), "depth" : 25 * mm});
        }
        {
            var Q0;
            Q0=makeQuery(id+"F8.imprint","IMPRINT",FACE,{"disambiguationData":[TD([[makeQuery(id+"F8.imprint","IMPRINT",EDGE,{"derivedFrom":sQuery(id+"F8.wireOp",EDGE,"E16")}),-1.0]])]});
            var Q1;
            Q1=makeQuery(id+"F2.opExtrude","CAP_FACE",FACE,{"disambiguationData":[OSD([sQuery(id+"F1.wireOp",EDGE,"E0.bottom"),sQuery(id+"F1.wireOp",EDGE,"E0.left"),sQuery(id+"F1.wireOp",EDGE,"E2"),sQuery(id+"F1.wireOp",EDGE,"E3"),sQuery(id+"F1.wireOp",EDGE,"E4.1.0.0"),sQuery(id+"F1.wireOp",EDGE,"E4.1.0.1"),sQuery(id+"F1.wireOp",EDGE,"E4.2.0.0"),sQuery(id+"F1.wireOp",EDGE,"E4.2.0.1"),sQuery(id+"F1.wireOp",EDGE,"E4.3.0.0"),sQuery(id+"F1.wireOp",EDGE,"E4.3.0.1"),sQuery(id+"F1.wireOp",EDGE,"E4.4.0.0"),sQuery(id+"F1.wireOp",EDGE,"E4.4.0.1"),sQuery(id+"F1.wireOp",EDGE,"E4.5.0.0"),sQuery(id+"F1.wireOp",EDGE,"E4.5.0.1"),sQuery(id+"F1.wireOp",EDGE,"E4.6.0.0"),sQuery(id+"F1.wireOp",EDGE,"E4.6.0.1"),sQuery(id+"F1.wireOp",EDGE,"E4.7.0.0"),sQuery(id+"F1.wireOp",EDGE,"E4.7.0.1"),sQuery(id+"F1.wireOp",EDGE,"E4.8.0.0"),sQuery(id+"F1.wireOp",EDGE,"E4.8.0.1"),sQuery(id+"F1.wireOp",EDGE,"E4.9.0.0"),sQuery(id+"F1.wireOp",EDGE,"E4.9.0.1"),sQuery(id+"F1.wireOp",EDGE,"E4.10.0.0"),sQuery(id+"F1.wireOp",EDGE,"E4.10.0.1"),sQuery(id+"F1.wireOp",EDGE,"E4.11.0.0"),sQuery(id+"F1.wireOp",EDGE,"E4.11.0.1"),sQuery(id+"F1.wireOp",EDGE,"E4.12.0.0"),sQuery(id+"F1.wireOp",EDGE,"E4.12.0.1"),sQuery(id+"F1.wireOp",EDGE,"E4.13.0.0"),sQuery(id+"F1.wireOp",EDGE,"E4.13.0.1"),sQuery(id+"F1.wireOp",EDGE,"E5"),sQuery(id+"F1.wireOp",EDGE,"E6"),sQuery(id+"F1.wireOp",EDGE,"E7")])],"isStart":false});
            extrude(context, id + "F12", {"entities" : qUnion([Q0]), "operationType" : NewBodyOperationType.ADD, "endBoundEntityFace" : qUnion([Q1]), "depth" : .6 * mm});
        }
    });
